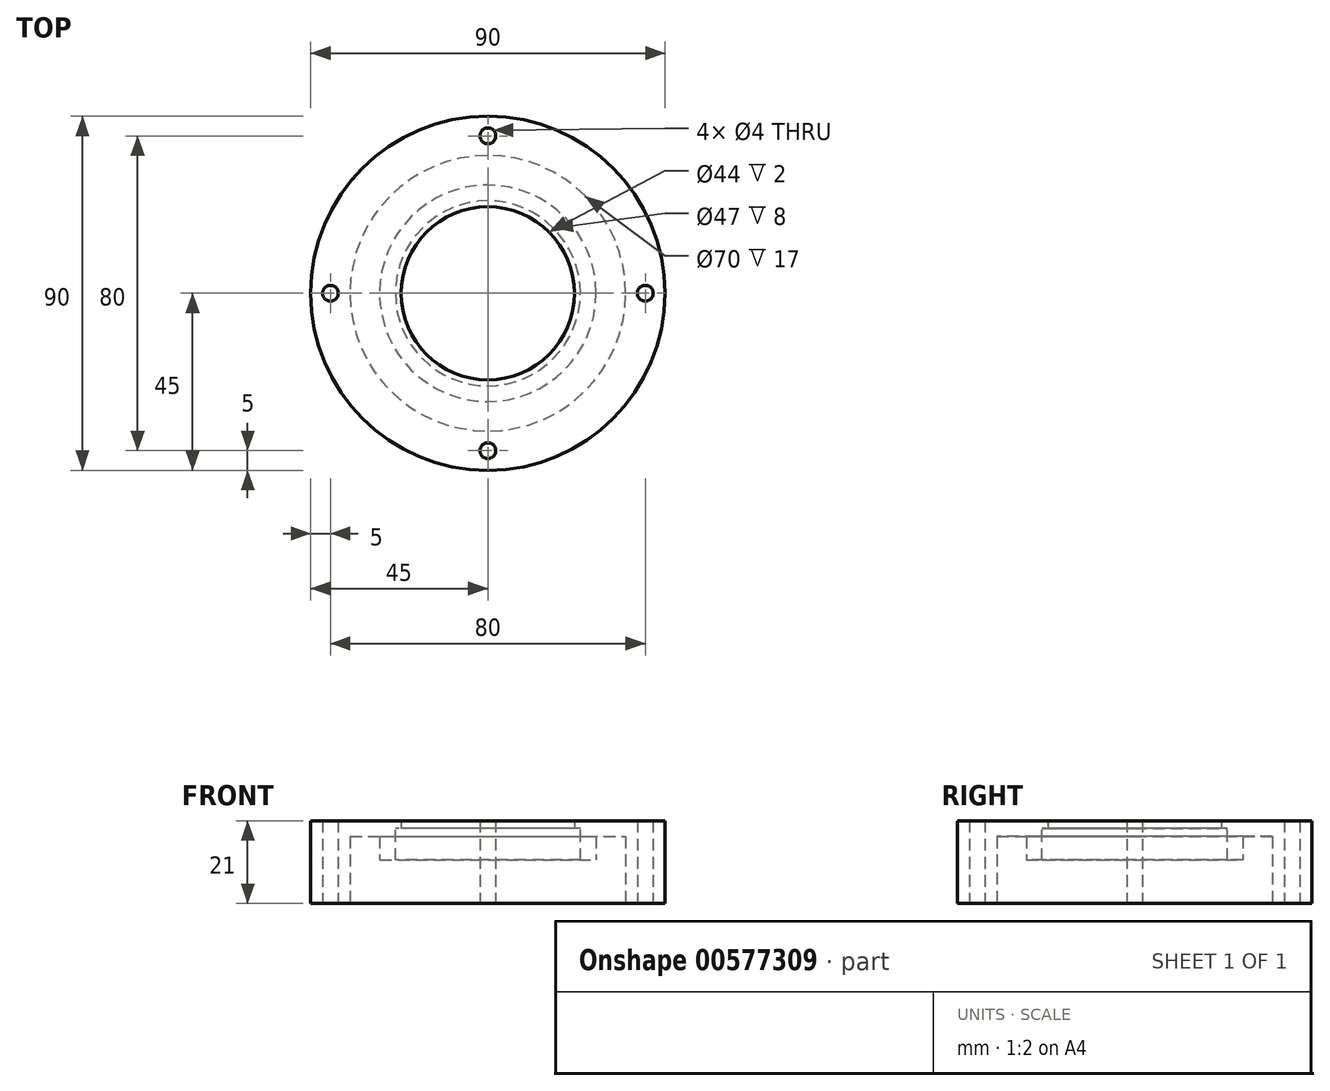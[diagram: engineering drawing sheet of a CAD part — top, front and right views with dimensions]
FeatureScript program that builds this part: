
annotation { "Feature Type Name" : "Feature", "Feature Type Description" : "" }
export const myFeature = defineFeature(function(context is Context, id is Id, definition is map)
    precondition{}
    {
        {
            var Q0;
            Q0=qCreatedBy(makeId("Top.planeOp"),FACE);
            var sketch = newSketch(context, id + "F0", { "sketchPlane" : qUnion([Q0])});
            skCircle(sketch, "E0", {"center": v(10, 29.8) * mm, "radius": 22 * mm});
            skCircle(sketch, "E1", {"center": v(10, 29.8) * mm, "radius": 23.5 * mm});
            skSolve(sketch);
        }
        {
            var Q0;
            Q0 = qSketchRegion(id + "F0", true);
            extrude(context, id + "F1", {"entities" : qUnion([Q0]), "depth" : 2 * mm, "offsetDistance" : 25 * mm});
        }
        {
            var Q0;
            Q0=makeQuery(id+"F1.opExtrude","CAP_FACE",FACE,{"disambiguationData":[OSD([sQuery(id+"F0.wireOp",EDGE,"E0"),sQuery(id+"F0.wireOp",EDGE,"E1")])],"isStart":false});
            var sketch = newSketch(context, id + "F2", { "sketchPlane" : qUnion([Q0])});
            skCircle(sketch, "E2", {"center": v(10, 29.8) * mm, "radius": 23.5 * mm});
            skCircle(sketch, "E3", {"center": v(10, 29.8) * mm, "radius": 45 * mm});
            skSolve(sketch);
        }
        {
            var Q0;
            Q0 = qSketchRegion(id + "F2", true);
            extrude(context, id + "F3", {"entities" : qUnion([Q0]), "operationType" : NewBodyOperationType.ADD, "oppositeDirection" : true, "depth" : 10 * mm, "offsetDistance" : 25 * mm});
        }
        {
            var Q0;
            Q0=makeQuery(id+"F3.opExtrude","CAP_FACE",FACE,{"disambiguationData":[OSD([sQuery(id+"F2.wireOp",EDGE,"E2"),sQuery(id+"F2.wireOp",EDGE,"E3")])],"isStart":false});
            var sketch = newSketch(context, id + "F4", { "sketchPlane" : qUnion([Q0])});
            skCircle(sketch, "E4", {"center": v(10, -29.8) * mm, "radius": 35 * mm});
            skCircle(sketch, "E5", {"center": v(10, -29.8) * mm, "radius": 27.5 * mm});
            skSolve(sketch);
        }
        {
            var Q0;
            Q0 = qSketchRegion(id + "F4", true);
            extrude(context, id + "F5", {"entities" : qUnion([Q0]), "operationType" : NewBodyOperationType.REMOVE, "oppositeDirection" : true, "depth" : 6 * mm, "offsetDistance" : 25 * mm});
        }
        {
            var Q0;
            {var subQ0=sQuery(id+"F2.wireOp",EDGE,"E3");Q0=makeQuery(id+"F5.boolean.opBoolean","SPLIT",FACE,{"disambiguationData":[TD([makeQuery(id+"F3.opExtrude","SWEPT_FACE",FACE,{"disambiguationData":[OSD([subQ0])]})])],"derivedFrom":makeQuery(id+"F3.opExtrude","CAP_FACE",FACE,{"disambiguationData":[OSD([sQuery(id+"F2.wireOp",EDGE,"E2"),subQ0])],"isStart":false})});}
            extrude(context, id + "F6", {"entities" : qUnion([Q0]), "operationType" : NewBodyOperationType.ADD, "depth" : 11 * mm, "offsetDistance" : 25 * mm});
        }
        {
            var Q0;
            Q0=makeQuery(id+"F6.opExtrude","CAP_FACE",FACE,{"disambiguationData":[OSD([sQuery(id+"F2.wireOp",EDGE,"E2"),sQuery(id+"F2.wireOp",EDGE,"E3")])],"isStart":false});
            var sketch = newSketch(context, id + "F7", { "sketchPlane" : qUnion([Q0])});
            skCircle(sketch, "E6", {"center": v(10, 10.2) * mm, "radius": 2 * mm});
            skLineSegment(sketch, "E7", {"start": v(10, -29.8) * mm, "end": v(10, 15.2) * mm, "construction": true});
            skCircle(sketch, "E8.1.0", {"center": v(-30, -29.8) * mm, "radius": 2 * mm});
            skCircle(sketch, "E8.2.0", {"center": v(10, -69.8) * mm, "radius": 2 * mm});
            skCircle(sketch, "E8.3.0", {"center": v(50, -29.8) * mm, "radius": 2 * mm});
            skPoint(sketch, "E8.center", {"position": v(10, -29.8) * mm});
            skSolve(sketch);
        }
        {
            var Q0;
            Q0 = qSketchRegion(id + "F7", true);
            extrude(context, id + "F8", {"entities" : qUnion([Q0]), "operationType" : NewBodyOperationType.REMOVE, "endBound" : BoundingType.THROUGH_ALL, "oppositeDirection" : true, "depth" : 25 * mm, "offsetDistance" : 25 * mm});
        }
    });
